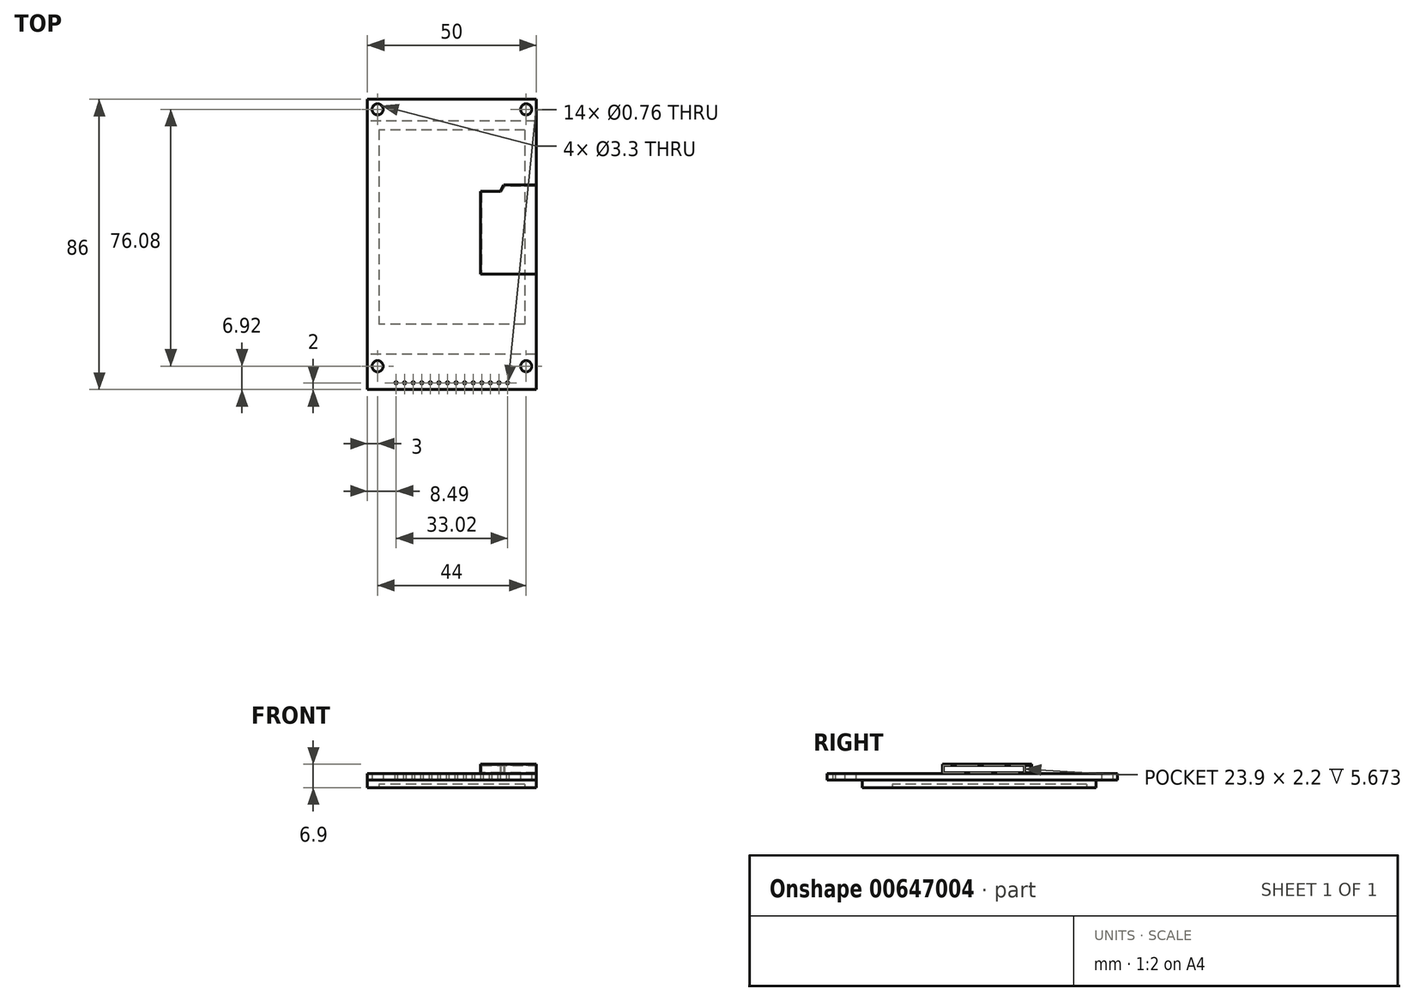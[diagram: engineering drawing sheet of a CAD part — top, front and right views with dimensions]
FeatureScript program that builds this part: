
annotation { "Feature Type Name" : "Feature", "Feature Type Description" : "" }
export const myFeature = defineFeature(function(context is Context, id is Id, definition is map)
    precondition{}
    {
        {
            var Q0;
            Q0=qCreatedBy(makeId("Top.planeOp"),FACE);
            var sketch = newSketch(context, id + "F0", { "sketchPlane" : qUnion([Q0])});
            skLineSegment(sketch, "E0.bottom", {"start": v(25, -43) * mm, "end": v(-25, -43) * mm});
            skLineSegment(sketch, "E0.top", {"start": v(25, 43) * mm, "end": v(-25, 43) * mm});
            skLineSegment(sketch, "E0.left", {"start": v(25, -43) * mm, "end": v(25, 43) * mm});
            skLineSegment(sketch, "E0.right", {"start": v(-25, -43) * mm, "end": v(-25, 43) * mm});
            skPoint(sketch, "E0.middle", {"position": v(0, 0) * mm});
            skCircle(sketch, "E1", {"center": v(-22, 40) * mm, "radius": 1.65 * mm});
            skCircle(sketch, "E2.0.1.0", {"center": v(-22, -36.08) * mm, "radius": 1.65 * mm});
            skCircle(sketch, "E2.1.0.0", {"center": v(22, 40) * mm, "radius": 1.65 * mm});
            skCircle(sketch, "E2.1.1.0", {"center": v(22, -36.08) * mm, "radius": 1.65 * mm});
            skLineSegment(sketch, "E2.direction1", {"start": v(-22, 40) * mm, "end": v(22, 40) * mm, "construction": true});
            skLineSegment(sketch, "E2.direction2", {"start": v(-22, 40) * mm, "end": v(-22, -36.08) * mm, "construction": true});
            skCircle(sketch, "E3", {"center": v(-16.5, -41) * mm, "radius": 0.38 * mm});
            skCircle(sketch, "E4.1.0.0", {"center": v(-13.97, -41) * mm, "radius": 0.38 * mm});
            skCircle(sketch, "E4.2.0.0", {"center": v(-11.43, -41) * mm, "radius": 0.38 * mm});
            skCircle(sketch, "E4.3.0.0", {"center": v(-8.89, -41) * mm, "radius": 0.38 * mm});
            skLineSegment(sketch, "E4.direction1", {"start": v(-16.5, -41) * mm, "end": v(-13.97, -41) * mm, "construction": true});
            skCircle(sketch, "E5.0.4.0", {"center": v(-6.35, -41) * mm, "radius": 0.38 * mm});
            skCircle(sketch, "E5.0.5.0", {"center": v(-3.8, -41) * mm, "radius": 0.38 * mm});
            skCircle(sketch, "E5.0.6.0", {"center": v(-1.27, -41) * mm, "radius": 0.38 * mm});
            skCircle(sketch, "E5.0.7.0", {"center": v(1.27, -41) * mm, "radius": 0.38 * mm});
            skCircle(sketch, "E5.0.8.0", {"center": v(3.81, -41) * mm, "radius": 0.38 * mm});
            skCircle(sketch, "E5.0.9.0", {"center": v(6.35, -41) * mm, "radius": 0.38 * mm});
            skCircle(sketch, "E5.0.10.0", {"center": v(8.9, -41) * mm, "radius": 0.38 * mm});
            skCircle(sketch, "E5.0.11.0", {"center": v(11.43, -41) * mm, "radius": 0.38 * mm});
            skCircle(sketch, "E5.0.12.0", {"center": v(13.97, -41) * mm, "radius": 0.38 * mm});
            skCircle(sketch, "E5.0.13.0", {"center": v(16.51, -41) * mm, "radius": 0.38 * mm});
            skSolve(sketch);
        }
        {
            var Q0;
            Q0=makeQuery(id+"F0.imprint","IMPRINT",FACE,{"disambiguationData":[TD([[makeQuery(id+"F0.imprint","IMPRINT",EDGE,{"derivedFrom":sQuery(id+"F0.wireOp",EDGE,"E0.bottom")}),-1.0]])]});
            extrude(context, id + "F1", {"entities" : qUnion([Q0]), "depth" : 1.8 * mm, "offsetDistance" : 25 * mm});
        }
        {
            var Q0;
            Q0=makeQuery(id+"F1.opExtrude","CAP_FACE",FACE,{"disambiguationData":[OSD([sQuery(id+"F0.wireOp",EDGE,"E0.bottom"),sQuery(id+"F0.wireOp",EDGE,"E0.top"),sQuery(id+"F0.wireOp",EDGE,"E0.left"),sQuery(id+"F0.wireOp",EDGE,"E0.right"),sQuery(id+"F0.wireOp",EDGE,"E1"),sQuery(id+"F0.wireOp",EDGE,"E2.0.1.0"),sQuery(id+"F0.wireOp",EDGE,"E2.1.0.0"),sQuery(id+"F0.wireOp",EDGE,"E2.1.1.0")])],"isStart":true});
            var sketch = newSketch(context, id + "F2", { "sketchPlane" : qUnion([Q0])});
            skLineSegment(sketch, "E6.bottom", {"start": v(25, -36.6) * mm, "end": v(-25, -36.6) * mm});
            skLineSegment(sketch, "E6.top", {"start": v(25, 32.6) * mm, "end": v(-25, 32.6) * mm});
            skLineSegment(sketch, "E6.left", {"start": v(25, -36.6) * mm, "end": v(25, 32.6) * mm});
            skLineSegment(sketch, "E6.right", {"start": v(-25, -36.6) * mm, "end": v(-25, 32.6) * mm});
            skSolve(sketch);
        }
        {
            var Q0;
            Q0=makeQuery(id+"F2.imprint","IMPRINT",FACE,{"disambiguationData":[TD([[makeQuery(id+"F2.imprint","IMPRINT",EDGE,{"derivedFrom":sQuery(id+"F2.wireOp",EDGE,"E6.bottom")}),-1.0]])]});
            extrude(context, id + "F3", {"entities" : qUnion([Q0]), "depth" : 2.3 * mm, "offsetDistance" : 25 * mm});
        }
        {
            var Q0;
            Q0=makeQuery(id+"F3.opExtrude","CAP_FACE",FACE,{"disambiguationData":[OSD([sQuery(id+"F2.wireOp",EDGE,"E6.bottom"),sQuery(id+"F2.wireOp",EDGE,"E6.top"),sQuery(id+"F2.wireOp",EDGE,"E6.left"),sQuery(id+"F2.wireOp",EDGE,"E6.right")])],"isStart":false});
            var sketch = newSketch(context, id + "F4", { "sketchPlane" : qUnion([Q0])});
            skLineSegment(sketch, "E7.bottom", {"start": v(21.6, -33.9) * mm, "end": v(-21.6, -33.9) * mm});
            skLineSegment(sketch, "E7.top", {"start": v(21.6, 23.7) * mm, "end": v(-21.6, 23.7) * mm});
            skLineSegment(sketch, "E7.left", {"start": v(21.6, -33.9) * mm, "end": v(21.6, 23.7) * mm});
            skLineSegment(sketch, "E7.right", {"start": v(-21.6, -33.9) * mm, "end": v(-21.6, 23.7) * mm});
            skPoint(sketch, "E7.middle", {"position": v(0, -5.1) * mm});
            skSolve(sketch);
        }
        {
            var Q0;
            Q0 = qSketchRegion(id + "F4", true);
            extrude(context, id + "F5", {"entities" : qUnion([Q0]), "operationType" : NewBodyOperationType.REMOVE, "oppositeDirection" : true, "depth" : 1 * mm, "offsetDistance" : 25 * mm});
        }
        {
            var Q0;
            Q0=makeQuery(id+"F1.opExtrude","CAP_FACE",FACE,{"disambiguationData":[OSD([sQuery(id+"F0.wireOp",EDGE,"E0.bottom"),sQuery(id+"F0.wireOp",EDGE,"E0.top"),sQuery(id+"F0.wireOp",EDGE,"E0.left"),sQuery(id+"F0.wireOp",EDGE,"E0.right"),sQuery(id+"F0.wireOp",EDGE,"E1"),sQuery(id+"F0.wireOp",EDGE,"E2.0.1.0"),sQuery(id+"F0.wireOp",EDGE,"E2.1.0.0"),sQuery(id+"F0.wireOp",EDGE,"E2.1.1.0"),sQuery(id+"F0.wireOp",EDGE,"E3"),sQuery(id+"F0.wireOp",EDGE,"E4.1.0.0"),sQuery(id+"F0.wireOp",EDGE,"E4.2.0.0"),sQuery(id+"F0.wireOp",EDGE,"E4.3.0.0"),sQuery(id+"F0.wireOp",EDGE,"E5.0.4.0"),sQuery(id+"F0.wireOp",EDGE,"E5.0.5.0"),sQuery(id+"F0.wireOp",EDGE,"E5.0.6.0"),sQuery(id+"F0.wireOp",EDGE,"E5.0.7.0"),sQuery(id+"F0.wireOp",EDGE,"E5.0.8.0"),sQuery(id+"F0.wireOp",EDGE,"E5.0.9.0"),sQuery(id+"F0.wireOp",EDGE,"E5.0.10.0"),sQuery(id+"F0.wireOp",EDGE,"E5.0.11.0"),sQuery(id+"F0.wireOp",EDGE,"E5.0.12.0"),sQuery(id+"F0.wireOp",EDGE,"E5.0.13.0")])],"isStart":false});
            var sketch = newSketch(context, id + "F6", { "sketchPlane" : qUnion([Q0])});
            skLineSegment(sketch, "E8", {"start": v(8.5, 15.7) * mm, "end": v(8.5, -8.8) * mm});
            skLineSegment(sketch, "E9", {"start": v(8.5, -8.8) * mm, "end": v(25, -8.8) * mm});
            skLineSegment(sketch, "E10", {"start": v(25, -8.8) * mm, "end": v(25, 17.6) * mm});
            skLineSegment(sketch, "E11", {"start": v(25, 17.6) * mm, "end": v(15.4, 17.6) * mm});
            skLineSegment(sketch, "E12", {"start": v(15.4, 17.6) * mm, "end": v(14.3, 15.7) * mm});
            skLineSegment(sketch, "E13", {"start": v(14.3, 15.7) * mm, "end": v(8.5, 15.7) * mm});
            skSolve(sketch);
        }
        {
            var Q0;
            Q0 = qSketchRegion(id + "F6", true);
            extrude(context, id + "F7", {"entities" : qUnion([Q0]), "depth" : 2.8 * mm, "offsetDistance" : 25 * mm});
        }
        {
            var Q0;
            Q0=makeQuery(id+"F7.opExtrude","SWEPT_FACE",FACE,{"disambiguationData":[OSD([sQuery(id+"F6.wireOp",EDGE,"E10")])]});
            shell(context, id + "F8", {"entities" : qUnion([Q0]), "thickness" : 0.3 * mm});
        }
    });
